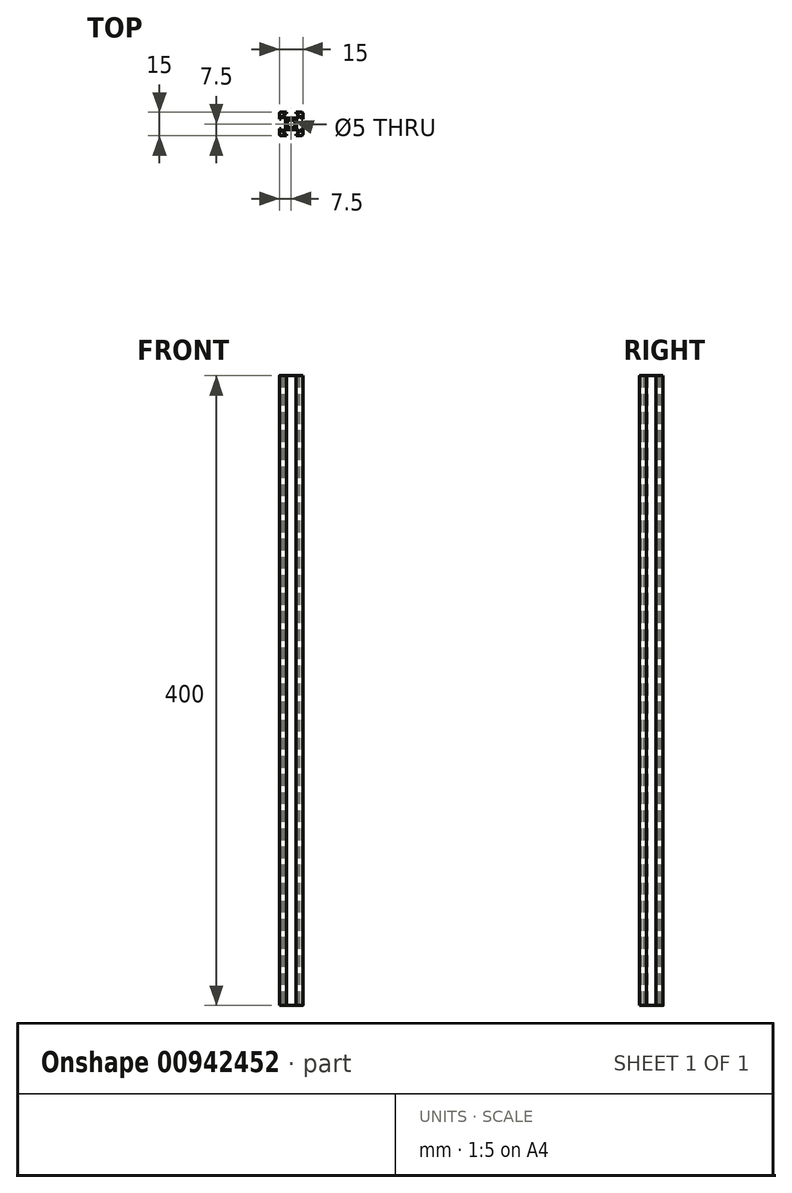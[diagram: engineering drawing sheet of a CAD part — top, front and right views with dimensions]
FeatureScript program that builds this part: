
annotation { "Feature Type Name" : "Feature", "Feature Type Description" : "" }
export const myFeature = defineFeature(function(context is Context, id is Id, definition is map)
    precondition{}
    {
        {
            assignVariable(context, id + "F0", {"name" : "height", "anyValue" : 400});
        }
        {
            var Q0;
            Q0=qCreatedBy(makeId("Top.planeOp"),FACE);
            var sketch = newSketch(context, id + "F1", { "sketchPlane" : qUnion([Q0])});
            skCircle(sketch, "E0", {"center": v(0, 0) * mm, "radius": 2.5 * mm});
            skLineSegment(sketch, "E1.bottom", {"start": v(6.5, 7.5) * mm, "end": v(3, 7.5) * mm});
            skLineSegment(sketch, "E1.top", {"start": v(6.5, -7.5) * mm, "end": v(3, -7.5) * mm});
            skLineSegment(sketch, "E1.left", {"start": v(7.5, 6.5) * mm, "end": v(7.5, 3) * mm});
            skLineSegment(sketch, "E1.right", {"start": v(-7.5, 6.5) * mm, "end": v(-7.5, 3) * mm});
            skPoint(sketch, "E2.visualSharp", {"position": v(-7.5, 7.5) * mm});
            skArc(sketch, "E2.filletArc", {"start": v(-6.5, 7.5) * mm, "mid": v(-7.2, 7.2) * mm, "end": v(-7.5, 6.5) * mm});
            skPoint(sketch, "E3.visualSharp", {"position": v(7.5, 7.5) * mm});
            skArc(sketch, "E3.filletArc", {"start": v(7.5, 6.5) * mm, "mid": v(7.2, 7.2) * mm, "end": v(6.5, 7.5) * mm});
            skPoint(sketch, "E4.visualSharp", {"position": v(7.5, -7.5) * mm});
            skArc(sketch, "E4.filletArc", {"start": v(6.5, -7.5) * mm, "mid": v(7.2, -7.2) * mm, "end": v(7.5, -6.5) * mm});
            skPoint(sketch, "E5.visualSharp", {"position": v(-7.5, -7.5) * mm});
            skArc(sketch, "E5.filletArc", {"start": v(-7.5, -6.5) * mm, "mid": v(-7.2, -7.2) * mm, "end": v(-6.5, -7.5) * mm});
            skLineSegment(sketch, "E6", {"start": v(-3, 7.5) * mm, "end": v(-3, 6.5) * mm});
            skLineSegment(sketch, "E7", {"start": v(3, 7.5) * mm, "end": v(3, 6.5) * mm});
            skLineSegment(sketch, "E8", {"start": v(-4.5, 6.5) * mm, "end": v(-4.5, 5) * mm});
            skLineSegment(sketch, "E9", {"start": v(4.5, 5) * mm, "end": v(4.5, 6.5) * mm});
            skLineSegment(sketch, "E10", {"start": v(4.5, 6.5) * mm, "end": v(3, 6.5) * mm});
            skLineSegment(sketch, "E11", {"start": v(-3, 3.5) * mm, "end": v(3, 3.5) * mm});
            skLineSegment(sketch, "E12", {"start": v(3, 3.5) * mm, "end": v(4.5, 5) * mm});
            skLineSegment(sketch, "E13", {"start": v(-3, 3.5) * mm, "end": v(-4.5, 5) * mm});
            skLineSegment(sketch, "E14.trimOffspring", {"start": v(-3, 6.5) * mm, "end": v(-4.5, 6.5) * mm});
            skLineSegment(sketch, "E15", {"start": v(-3, -7.5) * mm, "end": v(-3, -6.5) * mm});
            skLineSegment(sketch, "E16", {"start": v(-3, -6.5) * mm, "end": v(-4.5, -6.5) * mm});
            skLineSegment(sketch, "E17", {"start": v(-4.5, -6.5) * mm, "end": v(-4.5, -5) * mm});
            skLineSegment(sketch, "E18", {"start": v(-4.5, -5) * mm, "end": v(-3, -3.5) * mm});
            skLineSegment(sketch, "E19", {"start": v(-3, -3.5) * mm, "end": v(3, -3.5) * mm});
            skLineSegment(sketch, "E20", {"start": v(3, -3.5) * mm, "end": v(4.5, -5) * mm});
            skLineSegment(sketch, "E21", {"start": v(4.5, -5) * mm, "end": v(4.5, -6.5) * mm});
            skLineSegment(sketch, "E22", {"start": v(4.5, -6.5) * mm, "end": v(3, -6.5) * mm});
            skLineSegment(sketch, "E23", {"start": v(3, -6.5) * mm, "end": v(3, -7.5) * mm});
            skPoint(sketch, "E24", {"position": v(0, 7.5) * mm});
            skPoint(sketch, "E25", {"position": v(0, -7.5) * mm});
            skPoint(sketch, "E26", {"position": v(7.5, 0) * mm});
            skPoint(sketch, "E27", {"position": v(-7.5, 0) * mm});
            skLineSegment(sketch, "E28", {"start": v(7.5, 3) * mm, "end": v(6.5, 3) * mm});
            skLineSegment(sketch, "E29", {"start": v(6.5, 3) * mm, "end": v(6.5, 4.5) * mm});
            skLineSegment(sketch, "E30", {"start": v(6.5, 4.5) * mm, "end": v(5, 4.5) * mm});
            skLineSegment(sketch, "E31", {"start": v(5, 4.5) * mm, "end": v(3.5, 3) * mm});
            skLineSegment(sketch, "E32", {"start": v(3.5, 3) * mm, "end": v(3.5, -3) * mm});
            skLineSegment(sketch, "E33", {"start": v(3.5, -3) * mm, "end": v(5, -4.5) * mm});
            skLineSegment(sketch, "E34", {"start": v(5, -4.5) * mm, "end": v(6.5, -4.5) * mm});
            skLineSegment(sketch, "E35", {"start": v(6.5, -4.5) * mm, "end": v(6.5, -3) * mm});
            skLineSegment(sketch, "E36", {"start": v(6.5, -3) * mm, "end": v(7.5, -3) * mm});
            skLineSegment(sketch, "E37.trimOffspring", {"start": v(-3, 7.5) * mm, "end": v(-6.5, 7.5) * mm});
            skLineSegment(sketch, "E38.trimOffspring", {"start": v(7.5, -3) * mm, "end": v(7.5, -6.5) * mm});
            skLineSegment(sketch, "E39.trimOffspring", {"start": v(-3, -7.5) * mm, "end": v(-6.5, -7.5) * mm});
            skLineSegment(sketch, "E40", {"start": v(-7.5, 3) * mm, "end": v(-6.5, 3) * mm});
            skLineSegment(sketch, "E41", {"start": v(-6.5, 3) * mm, "end": v(-6.5, 4.5) * mm});
            skLineSegment(sketch, "E42", {"start": v(-6.5, 4.5) * mm, "end": v(-5, 4.5) * mm});
            skLineSegment(sketch, "E43", {"start": v(-5, 4.5) * mm, "end": v(-3.5, 3) * mm});
            skLineSegment(sketch, "E44", {"start": v(-3.5, 3) * mm, "end": v(-3.5, -3) * mm});
            skLineSegment(sketch, "E45", {"start": v(-3.5, -3) * mm, "end": v(-5, -4.5) * mm});
            skLineSegment(sketch, "E46", {"start": v(-5, -4.5) * mm, "end": v(-6.5, -4.5) * mm});
            skLineSegment(sketch, "E47", {"start": v(-6.5, -4.5) * mm, "end": v(-6.5, -3) * mm});
            skLineSegment(sketch, "E48", {"start": v(-6.5, -3) * mm, "end": v(-7.5, -3) * mm});
            skLineSegment(sketch, "E49.trimOffspring", {"start": v(-7.5, -3) * mm, "end": v(-7.5, -6.5) * mm});
            skSolve(sketch);
        }
        {
            var Q0;
            Q0=qSketchRegion(id+"F1",true);
            extrude(context, id + "F2", {"entities" : qUnion([Q0]), "depth" : (getVariable(context, 'height')) * mm, "offsetDistance" : 25 * mm});
        }
    });
